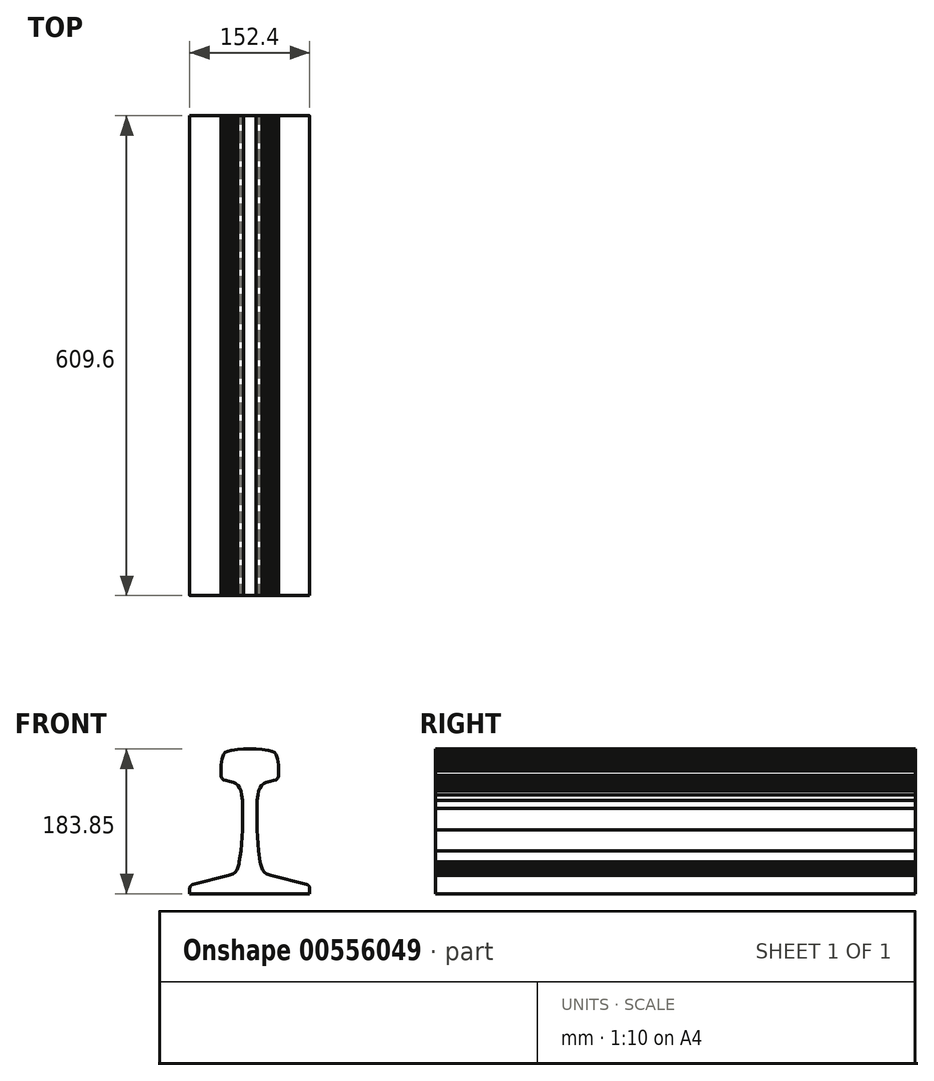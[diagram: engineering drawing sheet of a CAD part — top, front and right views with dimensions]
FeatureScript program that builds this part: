
annotation { "Feature Type Name" : "Feature", "Feature Type Description" : "" }
export const myFeature = defineFeature(function(context is Context, id is Id, definition is map)
    precondition{}
    {
        {
            var Q0;
            Q0=qCreatedBy(makeId("Front.planeOp"),FACE);
            var sketch = newSketch(context, id + "F0", { "sketchPlane" : qUnion([Q0])});
            skLineSegment(sketch, "E0", {"start": v(-76.2, -57.1) * mm, "end": v(76.2, -57.1) * mm});
            skLineSegment(sketch, "E1", {"start": v(-76.2, -57.1) * mm, "end": v(-76.2, -46.22) * mm});
            skLineSegment(sketch, "E2", {"start": v(-26.84, -33.73) * mm, "end": v(-76.2, -46.22) * mm});
            skPoint(sketch, "E3.startSnap0", {"position": v(0, -57.1) * mm});
            skPoint(sketch, "E3.endSnap0", {"position": v(0, -57.1) * mm});
            skLineSegment(sketch, "E4.MirrorCS", {"start": v(26.84, -33.73) * mm, "end": v(76.2, -46.22) * mm});
            skLineSegment(sketch, "E5.MirrorCS", {"start": v(0, -26.94) * mm, "end": v(0, -26.94) * mm});
            skLineSegment(sketch, "E6.MirrorCS", {"start": v(76.2, -57.1) * mm, "end": v(76.2, -46.22) * mm});
            skLineSegment(sketch, "E7", {"start": v(-26.84, -33.73) * mm, "end": v(-21.16, -31.84) * mm});
            skLineSegment(sketch, "E8", {"start": v(-21.16, -31.84) * mm, "end": v(-18.7, -29.61) * mm});
            skLineSegment(sketch, "E9", {"start": v(-18.7, -29.61) * mm, "end": v(-16.22, -26.55) * mm});
            skLineSegment(sketch, "E10", {"start": v(-16.22, -26.55) * mm, "end": v(-14.69, -22.9) * mm});
            skLineSegment(sketch, "E11", {"start": v(-14.69, -22.9) * mm, "end": v(-13.49, -19.14) * mm});
            skLineSegment(sketch, "E12", {"start": v(-13.49, -19.14) * mm, "end": v(-13.3, -16.85) * mm});
            skLineSegment(sketch, "E13", {"start": v(-13.3, -16.85) * mm, "end": v(-10.94, -2.66) * mm});
            skLineSegment(sketch, "E14", {"start": v(-10.94, -2.66) * mm, "end": v(-9.17, 23.94) * mm});
            skLineSegment(sketch, "E15", {"start": v(-9.17, 23.94) * mm, "end": v(-9.1, 51.27) * mm});
            skLineSegment(sketch, "E16", {"start": v(-9.1, 51.27) * mm, "end": v(-9.47, 61.37) * mm});
            skLineSegment(sketch, "E17", {"start": v(-36.63, 93.52) * mm, "end": v(-36.6, 93.52) * mm});
            skLineSegment(sketch, "E18", {"start": v(-9.47, 61.37) * mm, "end": v(-10.2, 68.53) * mm});
            skLineSegment(sketch, "E19", {"start": v(-10.2, 68.53) * mm, "end": v(-11.42, 73.4) * mm});
            skLineSegment(sketch, "E20", {"start": v(-11.42, 73.4) * mm, "end": v(-12.99, 77.66) * mm});
            skLineSegment(sketch, "E21", {"start": v(-12.99, 77.66) * mm, "end": v(-14.98, 80.45) * mm});
            skLineSegment(sketch, "E22", {"start": v(-14.98, 80.45) * mm, "end": v(-18.1, 83) * mm});
            skLineSegment(sketch, "E23", {"start": v(-18.1, 83) * mm, "end": v(-20.68, 84.15) * mm});
            skLineSegment(sketch, "E24", {"start": v(-20.68, 84.15) * mm, "end": v(-25.92, 85.98) * mm});
            skLineSegment(sketch, "E25", {"start": v(-25.92, 85.98) * mm, "end": v(-30.18, 87.13) * mm});
            skLineSegment(sketch, "E26", {"start": v(-30.18, 87.13) * mm, "end": v(-33.1, 87.75) * mm});
            skLineSegment(sketch, "E27", {"start": v(-33.1, 87.75) * mm, "end": v(-34.18, 88.3) * mm});
            skLineSegment(sketch, "E28", {"start": v(-34.18, 88.3) * mm, "end": v(-35.39, 89.62) * mm});
            skLineSegment(sketch, "E29", {"start": v(-35.39, 89.62) * mm, "end": v(-36.17, 91) * mm});
            skLineSegment(sketch, "E30", {"start": v(-36.17, 91) * mm, "end": v(-36.4, 91.97) * mm});
            skLineSegment(sketch, "E31", {"start": v(-36.4, 91.97) * mm, "end": v(-36.6, 93.51) * mm});
            skLineSegment(sketch, "E32", {"start": v(-36.6, 93.51) * mm, "end": v(-36.83, 98.88) * mm});
            skLineSegment(sketch, "E33", {"start": v(-36.83, 98.88) * mm, "end": v(-36.67, 103.67) * mm});
            skLineSegment(sketch, "E34", {"start": v(-36.67, 103.67) * mm, "end": v(-36.4, 106.65) * mm});
            skLineSegment(sketch, "E35", {"start": v(-36.4, 106.65) * mm, "end": v(-36.18, 110.32) * mm});
            skLineSegment(sketch, "E36", {"start": v(-36.18, 110.32) * mm, "end": v(-35.56, 114.28) * mm});
            skLineSegment(sketch, "E37", {"start": v(-35.56, 114.28) * mm, "end": v(-34.24, 117.98) * mm});
            skLineSegment(sketch, "E38", {"start": v(-34.24, 117.98) * mm, "end": v(-33.33, 119.88) * mm});
            skLineSegment(sketch, "E39", {"start": v(-33.33, 119.88) * mm, "end": v(-31.13, 122.46) * mm});
            skLineSegment(sketch, "E40", {"start": v(-31.13, 122.46) * mm, "end": v(-28.22, 124.04) * mm});
            skLineSegment(sketch, "E41", {"start": v(-28.22, 124.04) * mm, "end": v(-24.03, 125.35) * mm});
            skLineSegment(sketch, "E42", {"start": v(-24.03, 125.35) * mm, "end": v(-19.54, 126) * mm});
            skLineSegment(sketch, "E43.MirrorCS", {"start": v(36.4, 91.97) * mm, "end": v(36.6, 93.51) * mm});
            skLineSegment(sketch, "E44.MirrorCS", {"start": v(36.17, 91) * mm, "end": v(36.4, 91.97) * mm});
            skLineSegment(sketch, "E45.MirrorCS", {"start": v(13.49, -19.14) * mm, "end": v(13.3, -16.85) * mm});
            skLineSegment(sketch, "E46.MirrorCS", {"start": v(36.67, 103.67) * mm, "end": v(36.4, 106.65) * mm});
            skLineSegment(sketch, "E47.MirrorCS", {"start": v(20.68, 84.15) * mm, "end": v(25.92, 85.98) * mm});
            skLineSegment(sketch, "E48.MirrorCS", {"start": v(31.13, 122.46) * mm, "end": v(28.22, 124.04) * mm});
            skLineSegment(sketch, "E49.MirrorCS", {"start": v(36.6, 93.51) * mm, "end": v(36.83, 98.88) * mm});
            skLineSegment(sketch, "E50.MirrorCS", {"start": v(16.22, -26.55) * mm, "end": v(14.69, -22.9) * mm});
            skLineSegment(sketch, "E51.MirrorCS", {"start": v(34.18, 88.3) * mm, "end": v(35.39, 89.62) * mm});
            skLineSegment(sketch, "E52.MirrorCS", {"start": v(14.69, -22.9) * mm, "end": v(13.49, -19.14) * mm});
            skLineSegment(sketch, "E53.MirrorCS", {"start": v(12.99, 77.66) * mm, "end": v(14.98, 80.45) * mm});
            skLineSegment(sketch, "E54.MirrorCS", {"start": v(35.56, 114.28) * mm, "end": v(34.24, 117.98) * mm});
            skLineSegment(sketch, "E55.MirrorCS", {"start": v(28.22, 124.04) * mm, "end": v(24.03, 125.35) * mm});
            skLineSegment(sketch, "E56.MirrorCS", {"start": v(25.92, 85.98) * mm, "end": v(30.18, 87.13) * mm});
            skLineSegment(sketch, "E57.MirrorCS", {"start": v(26.84, -33.73) * mm, "end": v(21.16, -31.84) * mm});
            skLineSegment(sketch, "E58.MirrorCS", {"start": v(18.1, 83) * mm, "end": v(20.68, 84.15) * mm});
            skLineSegment(sketch, "E59.MirrorCS", {"start": v(21.16, -31.84) * mm, "end": v(18.7, -29.61) * mm});
            skLineSegment(sketch, "E60.MirrorCS", {"start": v(14.98, 80.45) * mm, "end": v(18.1, 83) * mm});
            skLineSegment(sketch, "E61.MirrorCS", {"start": v(33.1, 87.75) * mm, "end": v(34.18, 88.3) * mm});
            skLineSegment(sketch, "E62.MirrorCS", {"start": v(33.33, 119.88) * mm, "end": v(31.13, 122.46) * mm});
            skLineSegment(sketch, "E63.MirrorCS", {"start": v(30.18, 87.13) * mm, "end": v(33.1, 87.75) * mm});
            skLineSegment(sketch, "E64.MirrorCS", {"start": v(10.2, 68.53) * mm, "end": v(11.42, 73.4) * mm});
            skLineSegment(sketch, "E65.MirrorCS", {"start": v(34.24, 117.98) * mm, "end": v(33.33, 119.88) * mm});
            skLineSegment(sketch, "E66.MirrorCS", {"start": v(11.42, 73.4) * mm, "end": v(12.99, 77.66) * mm});
            skLineSegment(sketch, "E67.MirrorCS", {"start": v(24.03, 125.35) * mm, "end": v(19.54, 126) * mm});
            skLineSegment(sketch, "E68.MirrorCS", {"start": v(18.7, -29.61) * mm, "end": v(16.22, -26.55) * mm});
            skLineSegment(sketch, "E69.MirrorCS", {"start": v(35.39, 89.62) * mm, "end": v(36.17, 91) * mm});
            skLineSegment(sketch, "E70.MirrorCS", {"start": v(36.18, 110.32) * mm, "end": v(35.56, 114.28) * mm});
            skLineSegment(sketch, "E71.MirrorCS", {"start": v(36.4, 106.65) * mm, "end": v(36.18, 110.32) * mm});
            skLineSegment(sketch, "E72.MirrorCS", {"start": v(9.47, 61.37) * mm, "end": v(10.2, 68.53) * mm});
            skLineSegment(sketch, "E73.MirrorCS", {"start": v(15.45, 126.6) * mm, "end": v(15.43, 126.61) * mm});
            skLineSegment(sketch, "E74.MirrorCS", {"start": v(36.83, 98.88) * mm, "end": v(36.67, 103.67) * mm});
            skLineSegment(sketch, "E75.MirrorCS", {"start": v(10.94, -2.66) * mm, "end": v(9.17, 23.94) * mm});
            skLineSegment(sketch, "E76.MirrorCS", {"start": v(9.1, 51.27) * mm, "end": v(9.47, 61.37) * mm});
            skLineSegment(sketch, "E77.MirrorCS", {"start": v(13.3, -16.85) * mm, "end": v(10.94, -2.66) * mm});
            skLineSegment(sketch, "E78.MirrorCS", {"start": v(9.17, 23.94) * mm, "end": v(9.1, 51.27) * mm});
            skPoint(sketch, "E79.start.orphan", {"position": v(-15.43, 126.61) * mm});
            skLineSegment(sketch, "E80", {"start": v(-19.54, 126) * mm, "end": v(-15.43, 126.4) * mm});
            skLineSegment(sketch, "E81", {"start": v(-15.43, 126.4) * mm, "end": v(-8, 126.76) * mm});
            skLineSegment(sketch, "E82", {"start": v(-8, 126.76) * mm, "end": v(0, 126.76) * mm});
            skLineSegment(sketch, "E83.MirrorCS", {"start": v(8, 126.76) * mm, "end": v(0, 126.76) * mm});
            skLineSegment(sketch, "E84.MirrorCS", {"start": v(15.43, 126.4) * mm, "end": v(8, 126.76) * mm});
            skLineSegment(sketch, "E85.MirrorCS", {"start": v(19.54, 126) * mm, "end": v(15.43, 126.4) * mm});
            skPoint(sketch, "E86.orphan", {"position": v(-76.2, -26.94) * mm});
            skPoint(sketch, "E87.orphan", {"position": v(-31.72, -14.5) * mm});
            skPoint(sketch, "E88.end.orphan", {"position": v(-76.21, 41.14) * mm});
            skPoint(sketch, "E88.start.orphan", {"position": v(-76.21, -8.79) * mm});
            skLineSegment(sketch, "E89", {"start": v(76.2, -57.1) * mm, "end": v(76.2, -57.1) * mm});
            skPoint(sketch, "E90.orphan", {"position": v(76.2, -26.94) * mm});
            skPoint(sketch, "E91.MirrorCS.end.orphan", {"position": v(76.21, -8.79) * mm});
            skPoint(sketch, "E91.MirrorCS.start.orphan", {"position": v(31.72, -14.5) * mm});
            skPoint(sketch, "E92.orphan", {"position": v(0, -26.94) * mm});
            skLineSegment(sketch, "E93.trimOffspring", {"start": v(36.6, 93.52) * mm, "end": v(37.03, 93.52) * mm});
            skPoint(sketch, "E94.trimOffspring.end.orphan", {"position": v(0, 152.1) * mm});
            skPoint(sketch, "E3.start.orphan", {"position": v(0, -57.1) * mm});
            skSolve(sketch);
        }
        {
            var Q0;
            Q0=qSketchRegion(id+"F0",true);
            extrude(context, id + "F1", {"entities" : qUnion([Q0]), "depth" : 609.6 * mm, "offsetDistance" : 25.4 * mm});
        }
        {
            var Q0;
            Q0=makeQuery(id+"F1.opExtrude","SWEPT_EDGE",EDGE,{"disambiguationData":[OSD([sQuery(id+"F0.wireOp",EDGE,"E4.MirrorCS"),sQuery(id+"F0.wireOp",EDGE,"E6.MirrorCS")])]});
            var Q1;
            Q1=makeQuery(id+"F1.opExtrude","SWEPT_EDGE",EDGE,{"disambiguationData":[OSD([sQuery(id+"F0.wireOp",EDGE,"E1"),sQuery(id+"F0.wireOp",EDGE,"E2")])]});
            fillet(context, id + "F2", {"entities" : qUnion([Q0, Q1]), "radius" : 5.08 * mm, "tangentPropagation" : true, "allowEdgeOverflow" : false});
        }
    });
